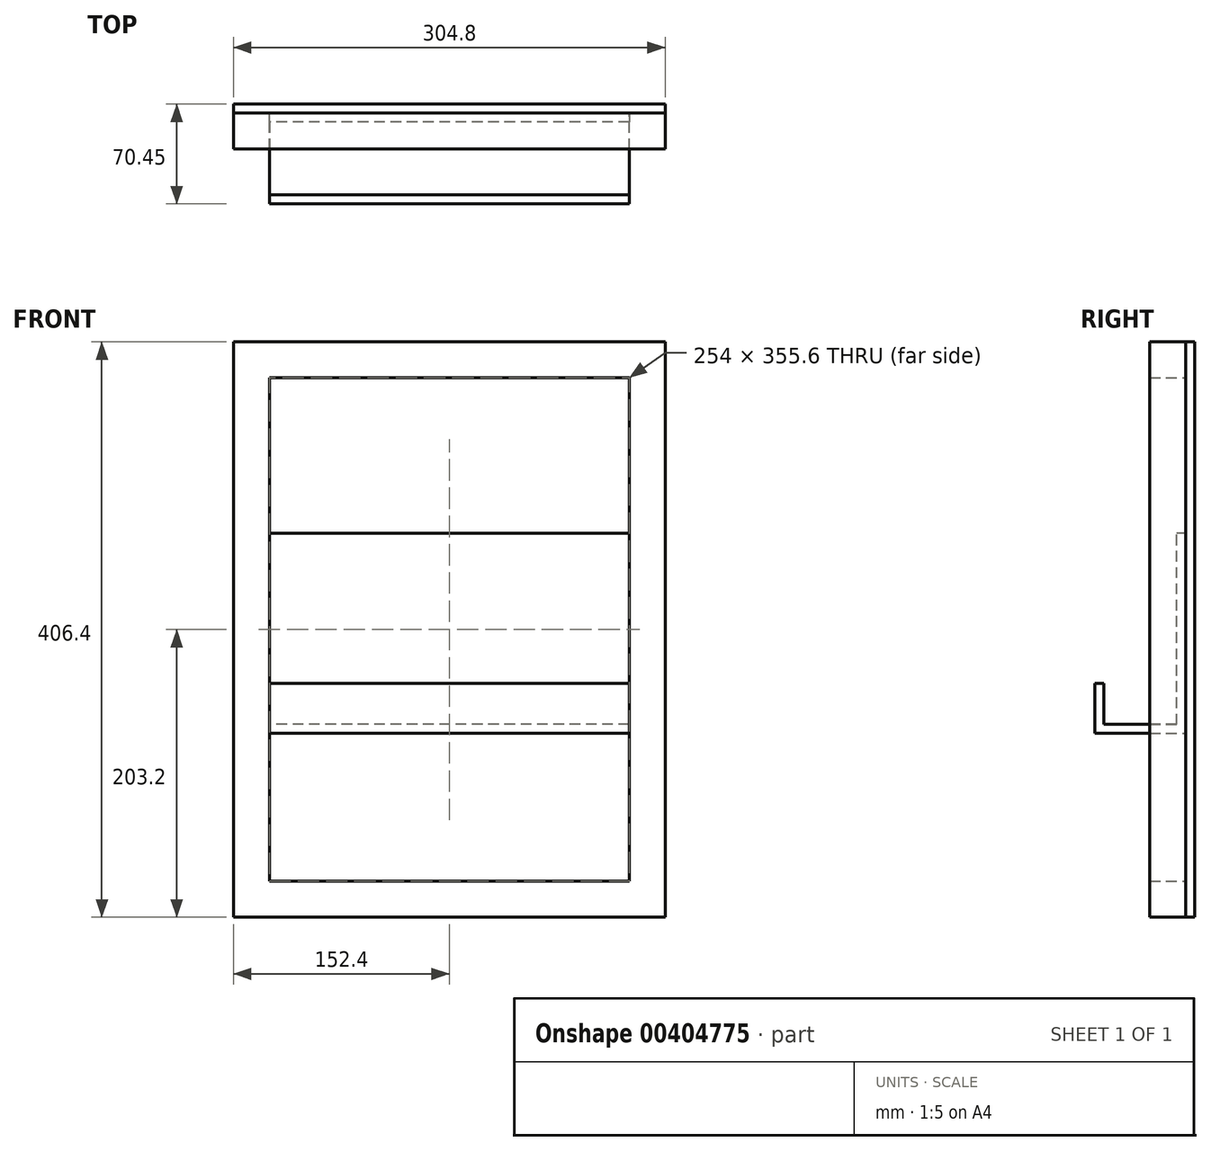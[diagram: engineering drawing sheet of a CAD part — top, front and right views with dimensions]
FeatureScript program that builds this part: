
annotation { "Feature Type Name" : "Feature", "Feature Type Description" : "" }
export const myFeature = defineFeature(function(context is Context, id is Id, definition is map)
    precondition{}
    {
        {
            var Q0;
            Q0=qCreatedBy(makeId("Front.planeOp"),FACE);
            var sketch = newSketch(context, id + "F0", { "sketchPlane" : qUnion([Q0])});
            skLineSegment(sketch, "E0.bottom", {"start": v(0, 0) * mm, "end": v(304.8, 0) * mm});
            skLineSegment(sketch, "E0.top", {"start": v(0, 406.4) * mm, "end": v(304.8, 406.4) * mm});
            skLineSegment(sketch, "E0.left", {"start": v(0, 0) * mm, "end": v(0, 406.4) * mm});
            skLineSegment(sketch, "E0.right", {"start": v(304.8, 0) * mm, "end": v(304.8, 406.4) * mm});
            skLineSegment(sketch, "E1.0", {"start": v(25.4, 25.4) * mm, "end": v(25.4, 381) * mm});
            skLineSegment(sketch, "E1.1", {"start": v(25.4, 25.4) * mm, "end": v(279.4, 25.4) * mm});
            skLineSegment(sketch, "E1.2", {"start": v(279.4, 25.4) * mm, "end": v(279.4, 381) * mm});
            skLineSegment(sketch, "E1.3", {"start": v(25.4, 381) * mm, "end": v(279.4, 381) * mm});
            skSolve(sketch);
        }
        {
            var Q0;
            Q0=makeQuery(id+"F0.imprint","IMPRINT",FACE,{"disambiguationData":[TD([[makeQuery(id+"F0.imprint","IMPRINT",EDGE,{"derivedFrom":sQuery(id+"F0.wireOp",EDGE,"E0.bottom")}),1.0]])]});
            extrude(context, id + "F1", {"entities" : qUnion([Q0]), "depth" : 25.4 * mm});
        }
        {
            var Q0;
            Q0=makeQuery(id+"F1.opExtrude","CAP_FACE",FACE,{"disambiguationData":[OSD([sQuery(id+"F0.wireOp",EDGE,"E0.bottom"),sQuery(id+"F0.wireOp",EDGE,"E0.top"),sQuery(id+"F0.wireOp",EDGE,"E0.left"),sQuery(id+"F0.wireOp",EDGE,"E0.right"),sQuery(id+"F0.wireOp",EDGE,"E1.0"),sQuery(id+"F0.wireOp",EDGE,"E1.1"),sQuery(id+"F0.wireOp",EDGE,"E1.2"),sQuery(id+"F0.wireOp",EDGE,"E1.3")])],"isStart":true});
            var sketch = newSketch(context, id + "F2", { "sketchPlane" : qUnion([Q0])});
            skLineSegment(sketch, "E2.bottom", {"start": v(-304.8, 0) * mm, "end": v(0, 0) * mm});
            skLineSegment(sketch, "E2.top", {"start": v(-304.8, 406.4) * mm, "end": v(0, 406.4) * mm});
            skLineSegment(sketch, "E2.left", {"start": v(-304.8, 0) * mm, "end": v(-304.8, 406.4) * mm});
            skLineSegment(sketch, "E2.right", {"start": v(0, 0) * mm, "end": v(0, 406.4) * mm});
            skSolve(sketch);
        }
        {
            var Q0;
            Q0 = qSketchRegion(id + "F2", true);
            extrude(context, id + "F3", {"entities" : qUnion([Q0]), "depth" : 6.35 * mm});
        }
        {
            var Q0;
            Q0=makeQuery(id+"F1.opExtrude","SWEPT_FACE",FACE,{"disambiguationData":[OSD([sQuery(id+"F0.wireOp",EDGE,"E1.0")])]});
            var sketch = newSketch(context, id + "F4", { "sketchPlane" : qUnion([Q0])});
            skLineSegment(sketch, "E3", {"start": v(0, 271.24) * mm, "end": v(0, 129.92) * mm});
            skLineSegment(sketch, "E4", {"start": v(0, 129.92) * mm, "end": v(-64.1, 129.92) * mm});
            skLineSegment(sketch, "E5", {"start": v(-64.1, 129.92) * mm, "end": v(-64.1, 165.36) * mm});
            skLineSegment(sketch, "E6.0", {"start": v(-57.75, 136.27) * mm, "end": v(-57.75, 165.36) * mm});
            skLineSegment(sketch, "E6.1", {"start": v(-6.35, 136.27) * mm, "end": v(-57.75, 136.27) * mm});
            skLineSegment(sketch, "E6.2", {"start": v(-6.35, 271.24) * mm, "end": v(-6.35, 136.27) * mm});
            skLineSegment(sketch, "E7", {"start": v(-64.1, 165.36) * mm, "end": v(-57.75, 165.36) * mm});
            skLineSegment(sketch, "E8", {"start": v(-6.35, 271.24) * mm, "end": v(0, 271.24) * mm});
            skSolve(sketch);
        }
        {
            var Q0;
            {var subQ4=sQuery(id+"F4.wireOp",EDGE,"E5");Q0=makeQuery(id+"F4.imprint","IMPRINT",FACE,{"disambiguationData":[TD([[makeQuery(id+"F4.imprint","IMPRINT",EDGE,{"derivedFrom":subQ4}),-1.0]])]});}
            var Q1;
            {var subQ2=sQuery(id+"F4.wireOp",EDGE,"E3");Q1=makeQuery(id+"F4.imprint","IMPRINT",FACE,{"disambiguationData":[TD([[makeQuery(id+"F4.imprint","IMPRINT",EDGE,{"derivedFrom":subQ2}),1.0]])]});}
            var Q2;
            Q2=makeQuery(id+"F1.opExtrude","SWEPT_FACE",FACE,{"disambiguationData":[OSD([sQuery(id+"F0.wireOp",EDGE,"E1.2")])]});
            extrude(context, id + "F5", {"entities" : qUnion([Q0, Q1]), "endBound" : BoundingType.UP_TO_SURFACE, "endBoundEntityFace" : qUnion([Q2]), "depth" : 25.4 * mm});
        }
    });
